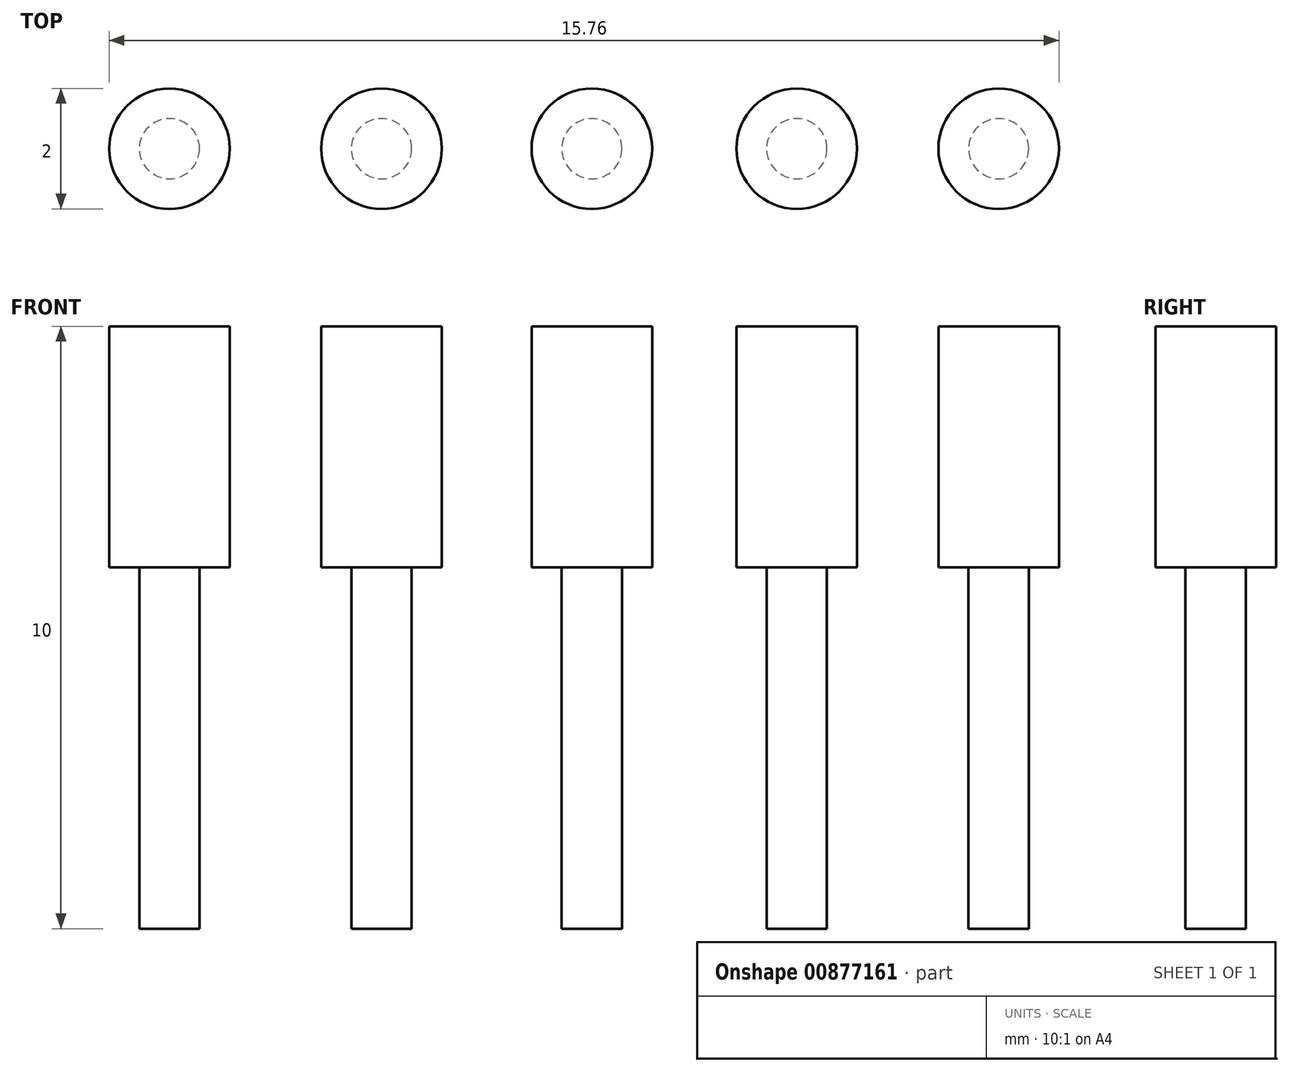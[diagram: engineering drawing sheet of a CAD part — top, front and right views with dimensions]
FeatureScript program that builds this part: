
annotation { "Feature Type Name" : "Feature", "Feature Type Description" : "" }
export const myFeature = defineFeature(function(context is Context, id is Id, definition is map)
    precondition{}
    {
        {
            var Q0;
            Q0=qCreatedBy(makeId("Front.planeOp"),FACE);
            var sketch = newSketch(context, id + "F0", { "sketchPlane" : qUnion([Q0])});
            skLineSegment(sketch, "E0", {"start": v(0, 0) * mm, "end": v(0, -6) * mm});
            skLineSegment(sketch, "E1", {"start": v(0, -6) * mm, "end": v(0.5, -6) * mm});
            skLineSegment(sketch, "E2", {"start": v(0.5, -6) * mm, "end": v(0.5, 0) * mm});
            skLineSegment(sketch, "E3", {"start": v(0.5, 0) * mm, "end": v(1, 0) * mm});
            skLineSegment(sketch, "E4", {"start": v(1, 0) * mm, "end": v(1, 4) * mm});
            skLineSegment(sketch, "E5", {"start": v(1, 4) * mm, "end": v(0, 4) * mm});
            skLineSegment(sketch, "E6", {"start": v(0, 4) * mm, "end": v(0, 0) * mm});
            skSolve(sketch);
        }
        {
            var Q0;
            Q0 = qSketchRegion(id + "F0", true);
            var Q1;
            Q1=sQuery(id+"F0.wireOp",EDGE,"E6");
            revolve(context, id + "F1", {"surfaceOperationType" : NewSurfaceOperationType.NEW, "entities" : qUnion([Q0]), "axis" : qUnion([Q1]), "revolveType" : RevolveType.FULL});
        }
        {
            var Q0;
            Q0=makeQuery(id+"F1.opRevolve","SWEPT_BODY",BODY,{"disambiguationData":[OSD([sQuery(id+"F0.wireOp",EDGE,"E0"),sQuery(id+"F0.wireOp",EDGE,"E1"),sQuery(id+"F0.wireOp",EDGE,"E2"),sQuery(id+"F0.wireOp",EDGE,"E3"),sQuery(id+"F0.wireOp",EDGE,"E4"),sQuery(id+"F0.wireOp",EDGE,"E5"),sQuery(id+"F0.wireOp",EDGE,"E6")])]});
            transform(context, id + "F2", {"entities" : qUnion([Q0]), "transformType" : TransformType.TRANSLATION_3D, "dx" : 3.52 * mm, "dy" : 0 * mm, "dz" : 0 * mm, "makeCopy" : true});
        }
        {
            var Q0;
            Q0=makeQuery(id+"F1.opRevolve","SWEPT_BODY",BODY,{"disambiguationData":[OSD([sQuery(id+"F0.wireOp",EDGE,"E0"),sQuery(id+"F0.wireOp",EDGE,"E1"),sQuery(id+"F0.wireOp",EDGE,"E2"),sQuery(id+"F0.wireOp",EDGE,"E3"),sQuery(id+"F0.wireOp",EDGE,"E4"),sQuery(id+"F0.wireOp",EDGE,"E5"),sQuery(id+"F0.wireOp",EDGE,"E6")])]});
            transform(context, id + "F3", {"entities" : qUnion([Q0]), "transformType" : TransformType.TRANSLATION_3D, "dx" : 7 * mm, "dy" : 0 * mm, "dz" : 0 * mm, "makeCopy" : true});
        }
        {
            var Q0;
            Q0=makeQuery(id+"F1.opRevolve","SWEPT_BODY",BODY,{"disambiguationData":[OSD([sQuery(id+"F0.wireOp",EDGE,"E0"),sQuery(id+"F0.wireOp",EDGE,"E1"),sQuery(id+"F0.wireOp",EDGE,"E2"),sQuery(id+"F0.wireOp",EDGE,"E3"),sQuery(id+"F0.wireOp",EDGE,"E4"),sQuery(id+"F0.wireOp",EDGE,"E5"),sQuery(id+"F0.wireOp",EDGE,"E6")])]});
            transform(context, id + "F4", {"entities" : qUnion([Q0]), "transformType" : TransformType.TRANSLATION_3D, "dx" : 10.4 * mm, "dy" : 0 * mm, "dz" : 0 * mm, "makeCopy" : true});
        }
        {
            var Q0;
            Q0=makeQuery(id+"F1.opRevolve","SWEPT_BODY",BODY,{"disambiguationData":[OSD([sQuery(id+"F0.wireOp",EDGE,"E0"),sQuery(id+"F0.wireOp",EDGE,"E1"),sQuery(id+"F0.wireOp",EDGE,"E2"),sQuery(id+"F0.wireOp",EDGE,"E3"),sQuery(id+"F0.wireOp",EDGE,"E4"),sQuery(id+"F0.wireOp",EDGE,"E5"),sQuery(id+"F0.wireOp",EDGE,"E6")])]});
            transform(context, id + "F5", {"entities" : qUnion([Q0]), "transformType" : TransformType.TRANSLATION_3D, "dx" : 13.76 * mm, "dy" : 0 * mm, "dz" : 0 * mm, "makeCopy" : true});
        }
    });
